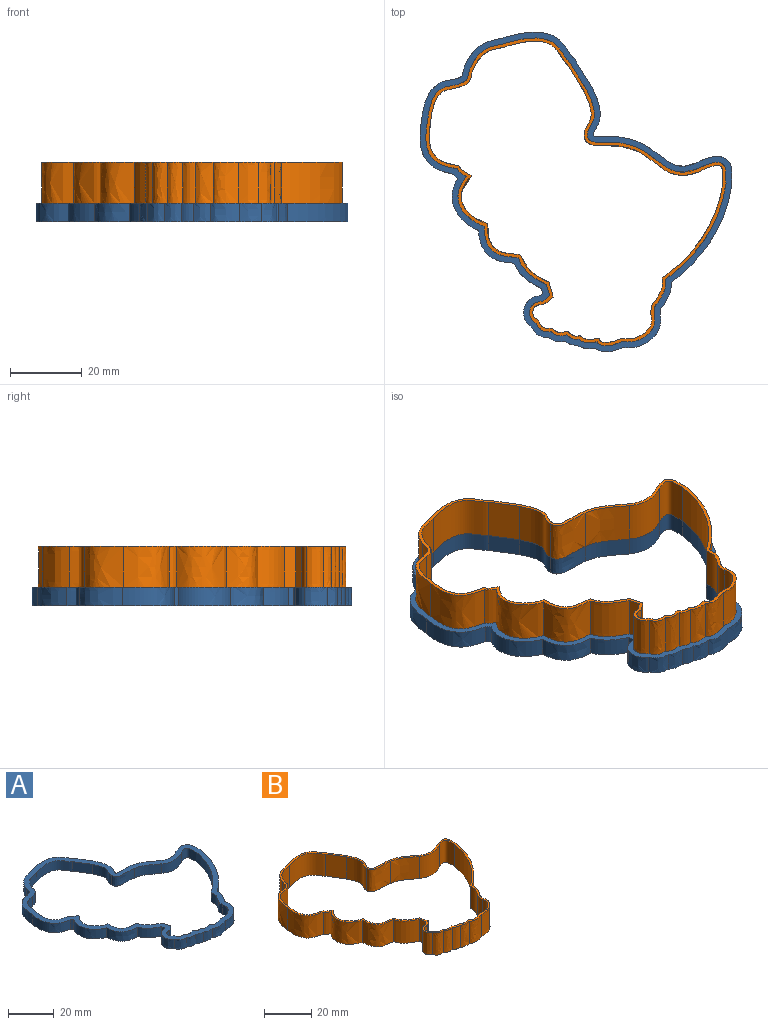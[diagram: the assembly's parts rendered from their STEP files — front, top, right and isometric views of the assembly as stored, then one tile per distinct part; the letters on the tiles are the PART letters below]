
ASSEMBLY  parts=2 mates=1
PART A: 62 faces, bbox 91.8x93.9x9.7 mm
  f0: plane 93.93x91.75mm, normal (0,0,1), area 740mm2, adj f2,f3,f4,f5,f6,f7,f8,f9
  f1: plane 93.93x91.75mm, normal (0,0,-1), area 740mm2, adj f2,f3,f4,f5,f6,f7,f8,f9
  f2: extruded ~5.08x1.3mm, area 6.6mm2, adj f0,f1,f26,f27
  f3: extruded ~8.65x5.08mm, area 44.2mm2, adj f0,f1,f4,f32
  f4: extruded ~5.08x0.2mm, area 1mm2, adj f0,f1,f3,f5
  f5: extruded ~13.26x5.08mm, area 71.3mm2, adj f0,f1,f4,f6
  f6: extruded ~8.01x5.08mm, area 47.9mm2, adj f0,f1,f5,f7
  f7: extruded ~19.38x7.5mm, area 114.9mm2, adj f0,f1,f6,f8
  f8: extruded ~11.33x8.31mm, area 75.6mm2, adj f0,f1,f7,f9
  f9: extruded ~5.08x3.39mm, area 25.5mm2, adj f0,f1,f8,f10
  f10: extruded ~12.21x9.15mm, area 86.3mm2, adj f0,f1,f9,f11
  f11: extruded ~14.37x9.36mm, area 99.4mm2, adj f0,f1,f10,f12
  f12: extruded ~5.08x1.19mm, area 8.5mm2, adj f0,f1,f11,f13
  f13: extruded ~14.54x7.38mm, area 92mm2, adj f0,f1,f12,f14
  f14: extruded ~9.91x9.14mm, area 77.5mm2, adj f0,f1,f13,f15
  f15: extruded ~7.66x7.13mm, area 54.4mm2, adj f0,f1,f14,f16
  f16: plane 5.08x1.43mm, normal (-0.96,-0.28,0), area 7.6mm2, adj f0,f1,f15,f17
  f17: plane 5.08x0.61mm, normal (-0.63,0.77,0), area 4mm2, adj f0,f1,f16,f18
  f18: extruded ~5.08x4.14mm, area 25.5mm2, adj f0,f1,f17,f19
  f19: extruded ~6.43x5.08mm, area 36.8mm2, adj f0,f1,f18,f20
  f20: extruded ~5.08x4.81mm, area 30.5mm2, adj f0,f1,f19,f21
  f21: extruded ~5.08x4.57mm, area 24.7mm2, adj f0,f1,f20,f22
  f22: extruded ~5.08x3.45mm, area 18.8mm2, adj f0,f1,f21,f23
  f23: extruded ~5.08x4.87mm, area 25.7mm2, adj f0,f1,f22,f24
  f24: extruded ~7.95x5.08mm, area 42.4mm2, adj f0,f1,f23,f25
  f25: extruded ~6.3x5.08mm, area 33.3mm2, adj f0,f1,f24,f26
  f26: extruded ~8.26x5.08mm, area 50.2mm2, adj f0,f1,f2,f25
  f27: extruded ~5.08x0.75mm, area 5.3mm2, adj f0,f1,f2,f28
  f28: extruded ~6.72x5.08mm, area 36.8mm2, adj f0,f1,f27,f29
  f29: extruded ~27.5x16.89mm, area 168.5mm2, adj f0,f1,f28,f30
  f30: extruded ~8.49x7.69mm, area 74mm2, adj f0,f1,f29,f31
  f31: extruded ~9.51x5.08mm, area 51.5mm2, adj f0,f1,f30,f32
  f32: extruded ~12.05x6.51mm, area 70.5mm2, adj f0,f1,f3,f31
  f33: extruded ~10.69x5.08mm, area 63mm2, adj f0,f1,f34,f61
  f34: extruded ~12.02x5.08mm, area 64.8mm2, adj f0,f1,f33,f35
  f35: extruded ~7.61x5.08mm, area 45.6mm2, adj f0,f1,f34,f36
  f36: extruded ~16.54x6.6mm, area 99.2mm2, adj f0,f1,f35,f37
  f37: extruded ~9.82x6.84mm, area 64.5mm2, adj f0,f1,f36,f38
  f38: extruded ~5.08x4.9mm, area 37.2mm2, adj f0,f1,f37,f39
  f39: extruded ~10.1x7.37mm, area 71.2mm2, adj f0,f1,f38,f40
  f40: extruded ~11.8x8.5mm, area 86.2mm2, adj f0,f1,f39,f41
  f41: extruded ~5.08x3.31mm, area 22.4mm2, adj f0,f1,f40,f42
  f42: extruded ~13.26x7.39mm, area 91.1mm2, adj f0,f1,f41,f43
  f43: extruded ~9.26x8.88mm, area 76.8mm2, adj f0,f1,f42,f44
  f44: extruded ~7.94x7.63mm, area 57.8mm2, adj f0,f1,f43,f45
  f45: plane 5.08x4.03mm, normal (0.96,0.28,0), area 21.3mm2, adj f0,f1,f44,f46
  f46: plane 5.08x2.6mm, normal (0.63,-0.77,0), area 17.1mm2, adj f0,f1,f45,f47
  f47: extruded ~5.08x2.82mm, area 16.1mm2, adj f0,f1,f46,f48
  f48: extruded ~5.08x3.48mm, area 21.4mm2, adj f0,f1,f47,f49
  f49: extruded ~5.08x3.87mm, area 25mm2, adj f0,f1,f48,f50
  f50: extruded ~5.08x4.33mm, area 24.3mm2, adj f0,f1,f49,f51
  f51: extruded ~5.08x3.48mm, area 20.3mm2, adj f0,f1,f50,f52
  f52: extruded ~5.13x5.08mm, area 28mm2, adj f0,f1,f51,f53
  f53: extruded ~6.41x5.08mm, area 36.5mm2, adj f0,f1,f52,f54
  f54: extruded ~5.35x5.08mm, area 28.1mm2, adj f0,f1,f53,f55
  f55: extruded ~5.84x5.08mm, area 35.9mm2, adj f0,f1,f54,f56
  f56: extruded ~5.08x3.86mm, area 21.7mm2, adj f0,f1,f55,f57
  f57: extruded ~6.37x5.08mm, area 34.6mm2, adj f0,f1,f56,f58
  f58: extruded ~26.25x16.93mm, area 163.3mm2, adj f0,f1,f57,f59
  f59: extruded ~5.15x5.08mm, area 48mm2, adj f0,f1,f58,f60
  f60: extruded ~12.05x5.08mm, area 65mm2, adj f0,f1,f59,f61
  f61: extruded ~11.13x6.11mm, area 65.3mm2, adj f0,f1,f33,f60
PART B: 60 faces, bbox 92.3x94.8x19.4 mm
  f0: plane 94.85x92.3mm, normal (0,0,1), area 255.6mm2, adj f2,f3,f4,f5,f6,f7,f8,f9
  f1: plane 94.85x92.3mm, normal (0,0,-1), area 255.6mm2, adj f2,f3,f4,f5,f6,f7,f8,f9
  f2: extruded ~11.43x9.98mm, area 127.8mm2, adj f0,f1,f3,f30
  f3: extruded ~12.45x11.43mm, area 151mm2, adj f0,f1,f2,f4
  f4: extruded ~11.43x7.75mm, area 104.4mm2, adj f0,f1,f3,f5
  f5: extruded ~17.54x11.43mm, area 235.5mm2, adj f0,f1,f4,f6
  f6: extruded ~11.43x10.35mm, area 154mm2, adj f0,f1,f5,f7
  f7: extruded ~11.43x4.37mm, area 74.7mm2, adj f0,f1,f6,f8
  f8: extruded ~11.43x10.84mm, area 171.9mm2, adj f0,f1,f7,f9
  f9: extruded ~12.68x11.43mm, area 203.5mm2, adj f0,f1,f8,f10
  f10: extruded ~11.43x2.59mm, area 39.2mm2, adj f0,f1,f9,f11
  f11: extruded ~13.83x11.43mm, area 205.7mm2, adj f0,f1,f10,f12
  f12: extruded ~11.43x9.45mm, area 171.9mm2, adj f0,f1,f11,f13
  f13: extruded ~11.43x7.88mm, area 128.2mm2, adj f0,f1,f12,f14
  f14: plane 11.43x3.13mm, normal (-0.96,-0.28,0), area 37.3mm2, adj f0,f1,f13,f15
  f15: plane 11.43x1.89mm, normal (-0.63,0.77,0), area 28mm2, adj f0,f1,f14,f16
  f16: extruded ~11.43x3.29mm, area 43.7mm2, adj f0,f1,f15,f17
  f17: extruded ~11.43x4.52mm, area 60.3mm2, adj f0,f1,f16,f18
  f18: extruded ~11.43x4.15mm, area 59.9mm2, adj f0,f1,f17,f19
  f19: extruded ~11.43x4.41mm, area 54.7mm2, adj f0,f1,f18,f20
  f20: extruded ~11.43x3.49mm, area 44.3mm2, adj f0,f1,f19,f21
  f21: extruded ~11.43x4.94mm, area 59.6mm2, adj f0,f1,f20,f22
  f22: extruded ~11.43x7.08mm, area 87.3mm2, adj f0,f1,f21,f23
  f23: extruded ~11.43x5.68mm, area 67.2mm2, adj f0,f1,f22,f24
  f24: extruded ~11.43x6.69mm, area 92.1mm2, adj f0,f1,f23,f25
  f25: extruded ~11.43x3.2mm, area 41mm2, adj f0,f1,f24,f26
  f26: extruded ~11.43x6.5mm, area 79.6mm2, adj f0,f1,f25,f27
  f27: extruded ~26.68x16.9mm, area 371.4mm2, adj f0,f1,f26,f28
  f28: extruded ~11.43x6.11mm, area 128.5mm2, adj f0,f1,f27,f29
  f29: extruded ~11.43x11.16mm, area 135.6mm2, adj f0,f1,f28,f30
  f30: extruded ~11.45x11.43mm, area 151mm2, adj f0,f1,f2,f29
  f31: extruded ~11.43x10.69mm, area 141.6mm2, adj f0,f1,f32,f59
  f32: extruded ~12.02x11.43mm, area 145.8mm2, adj f0,f1,f31,f33
  f33: extruded ~11.43x7.61mm, area 102.6mm2, adj f0,f1,f32,f34
  f34: extruded ~16.54x11.43mm, area 223.2mm2, adj f0,f1,f33,f35
  f35: extruded ~11.43x9.82mm, area 145.2mm2, adj f0,f1,f34,f36
  f36: extruded ~11.43x4.9mm, area 83.8mm2, adj f0,f1,f35,f37
  f37: extruded ~11.43x10.1mm, area 160.2mm2, adj f0,f1,f36,f38
  f38: extruded ~11.8x11.43mm, area 193.9mm2, adj f0,f1,f37,f39
  f39: extruded ~11.43x3.31mm, area 50.4mm2, adj f0,f1,f38,f40
  f40: extruded ~13.26x11.43mm, area 204.9mm2, adj f0,f1,f39,f41
  f41: extruded ~11.43x9.26mm, area 172.8mm2, adj f0,f1,f40,f42
  f42: extruded ~11.43x7.94mm, area 130mm2, adj f0,f1,f41,f43
  f43: plane 11.43x4.03mm, normal (0.96,0.28,0), area 48mm2, adj f0,f1,f42,f44
  f44: plane 11.43x2.6mm, normal (0.63,-0.77,0), area 38.4mm2, adj f0,f1,f43,f45
  f45: extruded ~11.43x2.82mm, area 36.2mm2, adj f0,f1,f44,f46
  f46: extruded ~11.43x3.48mm, area 48.1mm2, adj f0,f1,f45,f47
  f47: extruded ~11.43x3.87mm, area 56.3mm2, adj f0,f1,f46,f48
  f48: extruded ~11.43x4.33mm, area 54.7mm2, adj f0,f1,f47,f49
  f49: extruded ~11.43x3.48mm, area 45.7mm2, adj f0,f1,f48,f50
  f50: extruded ~11.43x5.13mm, area 63.1mm2, adj f0,f1,f49,f51
  f51: extruded ~11.43x6.41mm, area 82.1mm2, adj f0,f1,f50,f52
  f52: extruded ~11.43x5.35mm, area 63.2mm2, adj f0,f1,f51,f53
  f53: extruded ~11.43x5.84mm, area 80.7mm2, adj f0,f1,f52,f54
  f54: extruded ~11.43x3.86mm, area 48.9mm2, adj f0,f1,f53,f55
  f55: extruded ~11.43x6.37mm, area 77.7mm2, adj f0,f1,f54,f56
  f56: extruded ~26.25x16.93mm, area 367.5mm2, adj f0,f1,f55,f57
  f57: extruded ~11.43x5.15mm, area 108mm2, adj f0,f1,f56,f58
  f58: extruded ~12.05x11.43mm, area 146.3mm2, adj f0,f1,f57,f59
  f59: extruded ~11.43x11.13mm, area 147mm2, adj f0,f1,f31,f58
PLACE A t=(-90.8,59.51,27.26)mm
PLACE B t=(35.37,39.22,32.34)mm
MATE fastened B.f1 <-> A.f0  axis (0,0,1) through (3.81,43.59,32.34)mm
